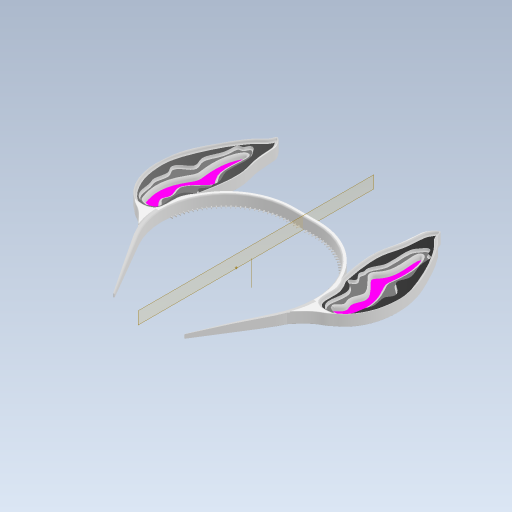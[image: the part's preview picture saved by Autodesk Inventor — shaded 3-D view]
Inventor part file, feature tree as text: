
AUTODESK INVENTOR PART (.ipt)
format: ipt  version: 2023 (Build 270158030, 158C)  size: 3,315,712 bytes
history: native  units: in
note: dims shown in document units (in); Inventor stores cm internally (conversion verified against a paired STEP export)
features: fillet x12, extrude x8, sketch x7, projected_geometry x6, other x1, pattern_circular x1, chamfer x1, mirror x1
ambient origin geometry x8: Origin, YZ Plane, XZ Plane, XY Plane, X Axis, Y Axis, Z Axis, Center Point
bodies: Solid1 (feature_tree)
feature tree (37):
  extrude  "Extrusion1"  Depth=0.1181in
  extrude  "Extrusion2"  Depth=0.3937in TaperAngle=0.0deg
  fillet  "Fillet2"  Radius=0.0433in
  other  "Work Axis1"
  pattern_circular  "Circular Pattern1"  Count=30  [1 undecoded]
  extrude  "Extrusion4"  Depth=4.3307in
  fillet  "Fillet6"  Radius=25.1969in
  fillet  "Fillet7"  Radius=0.7087in
  fillet  "Fillet8"  Radius=4.3307in
  extrude  "Extrusion10"  TaperAngle=0.0deg  [1 undecoded]
  extrude  "Extrusion11"  Depth=0.0394in
  extrude  "Extrusion12"  Depth=0.0236in
  extrude  "Extrusion14"  Depth=0.3937in TaperAngle=0.0deg
  fillet  "Fillet32"  Radius=0.3543in
  fillet  "Fillet33"  Radius=0.1969in
  fillet  "Fillet35"  Radius=0.0118in
  chamfer  "Chamfer2"  Distance=0.1181in
  fillet  "Fillet36"  Radius=0.0394in
  extrude  "Extrusion13"  Depth=0.015in TaperAngle=45.0deg
  fillet  "Fillet37"  Radius=0.7874in
  fillet  "Fillet38"  Radius=0.4331in
  fillet  "Fillet39"  Radius=2.3622in
  fillet  "Fillet40"  Radius=0.4331in
  mirror  "Mirror1"
  sketch  "Sketch1"  dims[d23=2.2638in d25=0.1181in]
  sketch  "Sketch2"  dims[d27=0.1181in d30=0.3937in d31=0.0in d48=0.0433in d49=0.0in]
  sketch  "Sketch13"  dims[d50=0.0118in]
  projected_geometry  "Projected Loop2"
  projected_geometry  "Projected Loop3"
  sketch  "Sketch14"  dims[d57=0.0787in d58=0.0157in d61=11.811in d62=-0.6184in]
  projected_geometry  "Projected Loop4"
  sketch  "Sketch16"  dims[d65=3.1496in d76=4.3307in d77=25.1969in d78=0.7087in d79=4.3307in]
  projected_geometry  "Projected Loop5"
  sketch  "Sketch18"  dims[d80=0.3937in d81=0.0in d82=0.0in]
  projected_geometry  "Projected Loop6"
  sketch  "Sketch20"  dims[d86=0.0394in d87=0.0394in d88=0.0236in d199=0.3937in d200=0.0in d201=0.3543in d202=0.0in d205=0.1969in d206=0.0in d209=0.0118in d210=0.1181in d212=0.0394in d213=0.015in d214=0.0787in d215=45.0deg d216=0.7874in d217=0.4331in d218=2.3622in d219=0.4331in d220=0.0984in d221=0.3937in d222=0.1181in d223=0.0787in d224=0.1969in d225=0.0in d226=0.0984in d227=0.0in d228=0.0354in d229=0.0472in d230=0.0118in d231=0.0157in]
  projected_geometry  "Projected Loop7"
note: 2 required parameter values undecoded (feature->parameter linkage not recoverable at this tier; creation-order binding heuristic only, values carry confidence <= 0.55)
